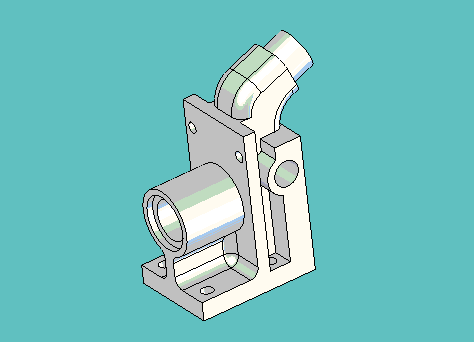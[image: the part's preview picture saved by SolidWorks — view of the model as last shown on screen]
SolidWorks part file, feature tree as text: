
SOLIDWORKS PART (.sldprt)
format: sldprt  version: not decoded by parser v0  size: 1,620,992 bytes
history: native  units: mm
features: sketch x21, boolean_combine x9, cut_extrude x9, extrude x8, fillet x3, revolve x2, material x1, chamfer x1, sweep x1 (+11 scaffold rows collapsed)
feature tree (66):
  scaffold x11  (default folders/planes/origin — collapsed)
  material  "Material <not specified>"
  sketch  "Sketch1"  dims[D1=4.7498mm D2=11.43mm D3=11.43mm D4=30.9626mm]
  extrude  "Extrude1"  Depth=41.275mm
  sketch  "Sketch5"  dims[D1=5.6515mm D2=5.6515mm D3=14.097mm]
  extrude  "Extrude7"  Depth=4.7752mm
  boolean_combine  "Combine4"
  sketch  "Sketch6"  dims[D2=7.0358mm D1=20.6502mm]
  extrude  "Extrude8"  Depth=38.1mm
  boolean_combine  "Combine5"
  sketch  "Sketch7"  dims[D1=10.16mm]
  extrude  "Extrude10"  Depth=22.2758mm
  boolean_combine  "Combine6"
  sketch  "Sketch8"  dims[D1=6.604mm D2=4.7752mm]
  extrude  "Extrude11"  Depth=17.4498mm
  boolean_combine  "Combine7"
  sketch  "Sketch9"  dims[c1.D3=6.5278mm c1.D1=28.956mm c1.D2=4.7625mm c2.D1=27.1272mm]
  extrude  "Extrude12"  Depth=38.1mm
  boolean_combine  "Combine8"
  sketch  "Sketch11"  dims[c1.D1=0.381mm c1.D2=3.175mm c2.D1=3.175mm c2.D3=0.254mm c2.D4=7.62mm c2.D2=0.381mm]
  revolve  "Revolve2"  Angle=360deg
  boolean_combine  "Combine11"
  sketch  "Sketch12"  dims[c1.D1=3.175mm c1.D2=3.175mm c1.D3=3.175mm c1.D7=3.175mm c1.D4=9.525mm c1.D5=7.9248mm c1.D6=7.9248mm c2.D7=26.9748mm c2.D8=26.9748mm c2.D4=26.9875mm c2.D3=7.9248mm c2.D6=9.525mm c2.D5=7.9248mm c3.D8=7.9248mm c3.D9=9.525mm c4.D8=7.9248mm]
  extrude  "Extrude14"  Depth=12.7mm
  boolean_combine  "Combine12"
  chamfer  "Chamfer1"  Distance=0.889mm Angle=15deg
  sketch  "Sketch21"  dims[D1=3.175mm D2=15.875mm]
  cut_extrude  "Cut-Extrude6"  [1 undecoded]
  sketch  "Sketch24"  dims[c1.D2=2.032mm c1.D3=~2.38125mm c1.D4=~2.38125mm c1.D5=3.175mm c1.D1=4.7625mm c2.D3=3.175mm c2.D4=1.5875mm c2.D5=1.5875mm c2.D1=0.0mm]
  cut_extrude  "Cut-Extrude9"  [1 undecoded]
  fillet  "Fillet1"  Radius=2.38125mm
  sketch  "Sketch25"  dims[c1.D2=6.5278mm c1.D1=3.175mm c2.D2=22.225mm c2.D3=6.35mm c3.D2=1.778mm c3.D4=3.175mm c3.D5=7.9375mm c4.D4=31.75mm]
  cut_extrude  "Cut-Extrude10"  Depth=5.55625mm
  sketch  "Sketch26"  dims[D1=0.0mm]
  cut_extrude  "Cut-Extrude11"  Depth=5.55625mm
  sketch  "Sketch27"  dims[D3=2.7051mm D5=2.7051mm D1=34.925mm D2=8.89mm D4=8.89mm]
  cut_extrude  "Cut-Extrude12"  [1 undecoded]
  sketch  "Sketch29"  dims[D1=0.0mm]
  cut_extrude  "Cut-Extrude14"  Depth=6.35mm
  sketch  "Sketch30"
  sketch  "Sketch31"  dims[c1.D1=~20.20113mm c2.D1=68.0deg c2.D2=12.7mm c2.D3=6.35mm c2.D4=4.953mm c2.D5=4.953mm]
  sweep  "Sweep1"
  sketch  "Sketch32"  dims[c1.D1=9.525mm c1.D4=5.08mm c1.D3=6.35mm c2.D1=~7.666823mm c3.D1=54.0deg c3.D2=~15.09935mm c4.D2=42.0deg c4.D1=5.08mm c5.D2=5.08mm c5.D3=6.35mm c5.D1=~5.87502mm c6.D2=~5.87502mm]
  extrude  "Extrude15"  [1 undecoded]
  boolean_combine  "Combine13"
  boolean_combine  "Combine14"
  sketch  "Sketch33"  dims[D1=7.1628mm]
  cut_extrude  "Cut-Extrude15"  Depth=6.35mm
  sketch  "Sketch34"  dims[D2=10.414mm D3=3.175mm D4=3.175mm D1=0.0mm]
  cut_extrude  "Cut-Extrude16"  Depth=6.35mm
  fillet  "Fillet2"  Radius=3.175mm
  fillet  "Fillet3"  Radius=0.79375mm
  sketch  "Sketch35"  dims[c1.D1=20.6502mm c1.D2=0.508mm c1.D3=3.4022mm c1.D4=7.366mm c1.D5=~0.736288mm c2.D5=15.0deg c2.D6=0.7112mm c2.D7=~2.324864mm c3.D7=~72.187055deg c4.D7=~1.885774mm]
  revolve  "Revolve3"  Angle=360deg
  sketch  "Sketch37"  dims[D1=13.5128mm]
  cut_extrude  "Cut-Extrude18"  Depth=1.5875mm
decode coverage: 39 of 54 modeling features carry decoded parameters
note: ~ marks probable driven/reference dimensions
note: 4 parameter values undecoded
summary: no parameter record found for 4 features
note: suppression state not decoded; provenance and decode notes live in map.json
